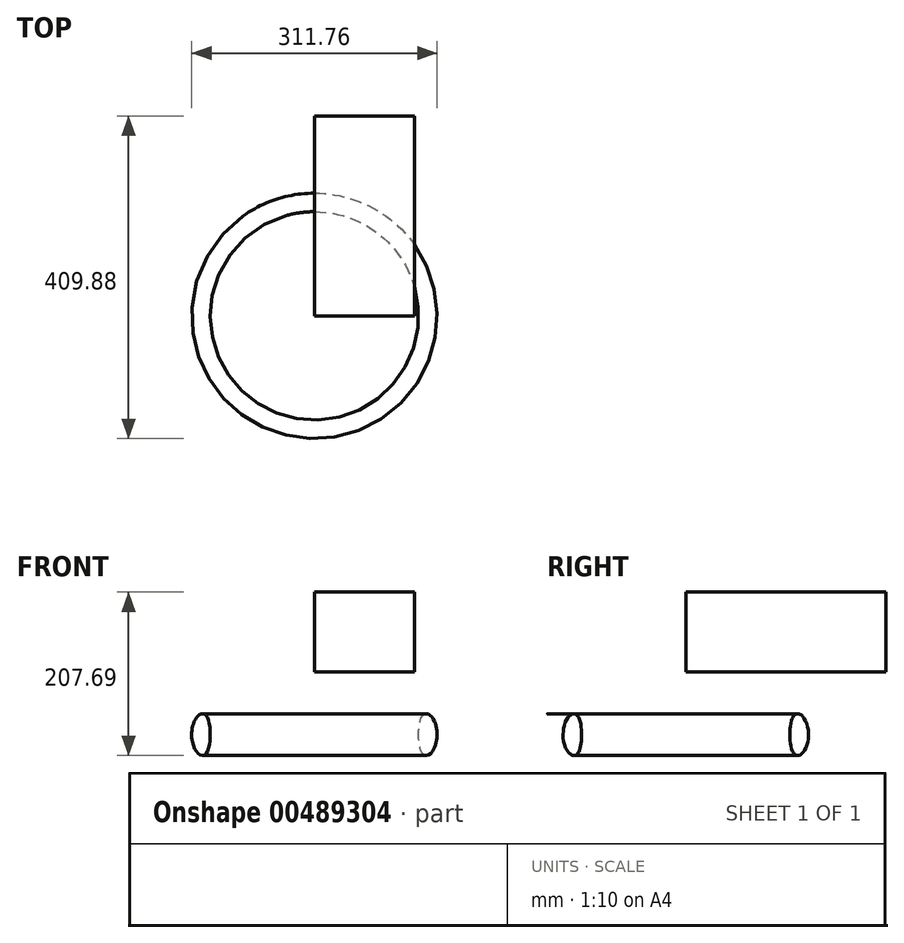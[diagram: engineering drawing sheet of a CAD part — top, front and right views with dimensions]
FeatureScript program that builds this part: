
annotation { "Feature Type Name" : "Feature", "Feature Type Description" : "" }
export const myFeature = defineFeature(function(context is Context, id is Id, definition is map)
    precondition{}
    {
        {
            var Q0;
            Q0=qCreatedBy(makeId("Front.planeOp"),FACE);
            var sketch = newSketch(context, id + "F0", { "sketchPlane" : qUnion([Q0])});
            skLineSegment(sketch, "E0.bottom", {"start": v(-25.52, -16.4) * mm, "end": v(101.48, -16.4) * mm});
            skLineSegment(sketch, "E0.top", {"start": v(-25.52, 85.2) * mm, "end": v(101.48, 85.2) * mm});
            skLineSegment(sketch, "E0.left", {"start": v(-25.52, -16.4) * mm, "end": v(-25.52, 85.2) * mm});
            skLineSegment(sketch, "E0.right", {"start": v(101.48, -16.4) * mm, "end": v(101.48, 85.2) * mm});
            skSolve(sketch);
        }
        {
            var Q0;
            Q0=makeQuery(id+"F0.imprint","IMPRINT",FACE,{"disambiguationData":[TD([[makeQuery(id+"F0.imprint","IMPRINT",EDGE,{"derivedFrom":sQuery(id+"F0.wireOp",EDGE,"E0.bottom")}),1.0]])]});
            extrude(context, id + "F1", {"entities" : qUnion([Q0]), "endBound" : BoundingType.SYMMETRIC, "depth" : 254 * mm});
        }
        {
            var Q0;
            Q0=qCreatedBy(makeId("Front.planeOp"),FACE);
            var sketch = newSketch(context, id + "F2", { "sketchPlane" : qUnion([Q0])});
            skCircle(sketch, "E1", {"center": v(-89.29, -95.89) * mm, "radius": 26.62 * mm});
            skSolve(sketch);
        }
        {
            var Q0;
            Q0=makeQuery(id+"F2.imprint","IMPRINT",FACE,{"disambiguationData":[TD([[makeQuery(id+"F2.imprint","IMPRINT",EDGE,{"derivedFrom":sQuery(id+"F2.wireOp",EDGE,"E1")}),1.0]])]});
            var Q1;
            Q1=makeQuery(id+"F1.opExtrude","CAP_EDGE",EDGE,{"disambiguationData":[OSD([sQuery(id+"F0.wireOp",EDGE,"E0.left")])],"isStart":false});
            revolve(context, id + "F3", {"entities" : qUnion([Q0]), "axis" : qUnion([Q1]), "revolveType" : RevolveType.FULL});
        }
    });
